# Revit family: Verano_V905_Iseo_GM_R21
name_source: partatom
category: Generic Models
units: mm (PartAtom-declared; Revit-internal decimal feet)

## family parameters
Always vertical = Yes
Can host rebar = No
Cut with Voids When Loaded = No
Part Type = Normal
Room Calculation Point = No
Round Connector Dimension = Use Diameter
Shared = No
Work Plane-Based = No

## types (2) — shared parameters
Achtung = Keine Garantie auf Wasserdichtigkeit bei einem Gefälle von weniger als 7º
Attention = Water resistance is not guaranteed on slopes less than 7º
Description = De terrasoverkapping Iseo is enorm geschikt model wanneer je met een lager budget op zoek bent naar een kwalitatief uitstekend type. De dakplaten van polycarbonaat zijn stevig en hebben een hoge slagvastheid zodat jij jarenlang kunt genieten van jouw overkapping.
Manufacturer = Verano Systems
Maximal Angle = 21.00°
Maximal Projection = 4000 mm  [stored 13.1234 ft]
Maximal Width = 14000 mm  [stored 45.9318 ft]
Minimal Angle = 5.00°
Minimal Projection = 2000 mm  [stored 6.56168 ft]
Minimal Width = 3000 mm  [stored 9.84252 ft]
Model = V905 Iseo
URL = https://verano.nl
zero-valued in all types: Default Elevation

## per-type parameters (varying)
| type | Classic Profile | Standard Profile |
| T2 - Classic Profile | Yes | No |
| T1 - Standard Profile | No | Yes |

note: [stored X ft] marks values corroborated as IEEE doubles in the binary element streams (Revit-internal decimal feet)

## geometry (parser evidence)
native form markers: Extrusion x9, Sweep x24
no freeform markers — native parametric forms only
